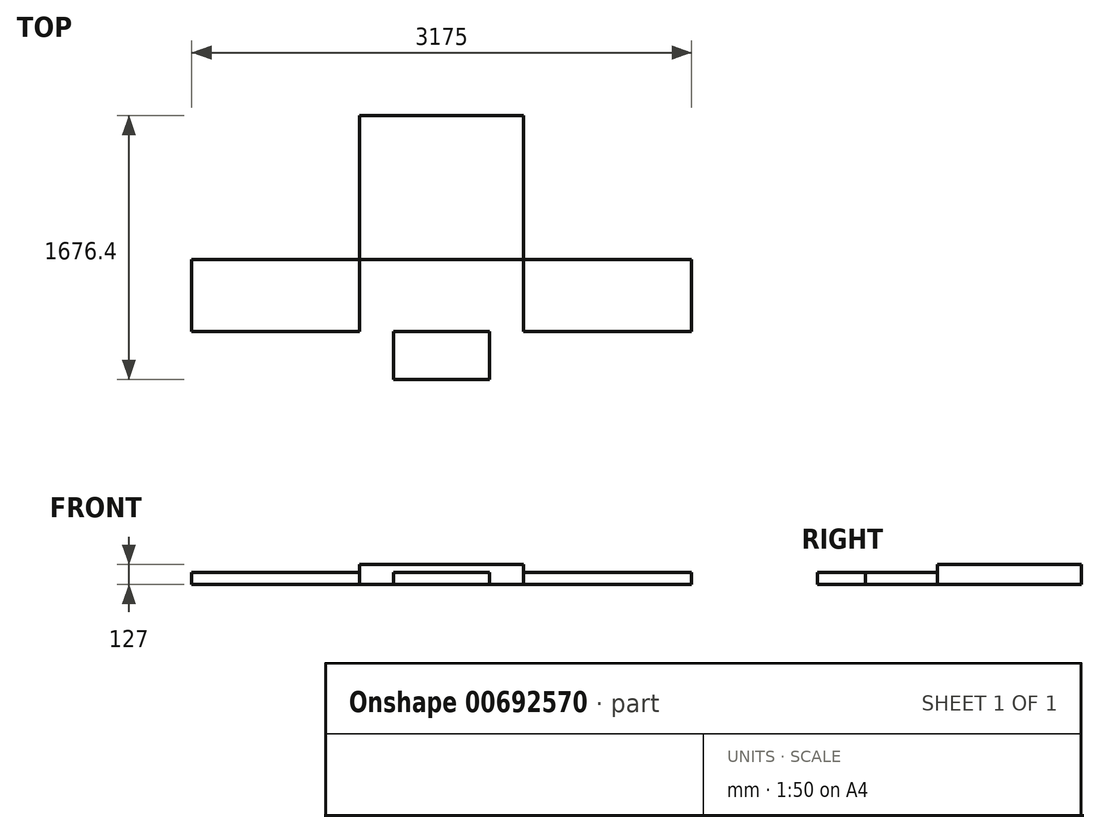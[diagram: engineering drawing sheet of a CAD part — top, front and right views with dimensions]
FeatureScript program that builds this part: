
annotation { "Feature Type Name" : "Feature", "Feature Type Description" : "" }
export const myFeature = defineFeature(function(context is Context, id is Id, definition is map)
    precondition{}
    {
        {
            var Q0;
            Q0=qCreatedBy(makeId("Top.planeOp"),FACE);
            var sketch = newSketch(context, id + "F0", { "sketchPlane" : qUnion([Q0])});
            skLineSegment(sketch, "E0.bottom", {"start": v(0, 0) * mm, "end": v(1041.4, 0) * mm});
            skLineSegment(sketch, "E0.top", {"start": v(0, 914.4) * mm, "end": v(1041.4, 914.4) * mm});
            skLineSegment(sketch, "E0.left", {"start": v(0, 0) * mm, "end": v(0, 914.4) * mm});
            skLineSegment(sketch, "E0.right", {"start": v(1041.4, 0) * mm, "end": v(1041.4, 914.4) * mm});
            skSolve(sketch);
        }
        {
            var Q0;
            Q0 = qSketchRegion(id + "F0", true);
            extrude(context, id + "F1", {"entities" : qUnion([Q0]), "depth" : 127 * mm, "offsetDistance" : 25.4 * mm});
        }
        {
            var Q0;
            Q0=makeQuery(id+"F1.opExtrude","CAP_FACE",FACE,{"disambiguationData":[OSD([sQuery(id+"F0.wireOp",EDGE,"E0.bottom"),sQuery(id+"F0.wireOp",EDGE,"E0.top"),sQuery(id+"F0.wireOp",EDGE,"E0.left"),sQuery(id+"F0.wireOp",EDGE,"E0.right")])],"isStart":false});
            var sketch = newSketch(context, id + "F2", { "sketchPlane" : qUnion([Q0])});
            skLineSegment(sketch, "E1.bottom", {"start": v(0, 0) * mm, "end": v(-1066.8, 0) * mm});
            skLineSegment(sketch, "E1.top", {"start": v(0, -457.2) * mm, "end": v(-1066.8, -457.2) * mm});
            skLineSegment(sketch, "E1.left", {"start": v(0, 0) * mm, "end": v(0, -457.2) * mm});
            skLineSegment(sketch, "E1.right", {"start": v(-1066.8, 0) * mm, "end": v(-1066.8, -457.2) * mm});
            skLineSegment(sketch, "E2.bottom", {"start": v(1041.4, 0) * mm, "end": v(2108.2, 0) * mm});
            skLineSegment(sketch, "E2.top", {"start": v(1041.4, -457.2) * mm, "end": v(2108.2, -457.2) * mm});
            skLineSegment(sketch, "E2.left", {"start": v(1041.4, 0) * mm, "end": v(1041.4, -457.2) * mm});
            skLineSegment(sketch, "E2.right", {"start": v(2108.2, 0) * mm, "end": v(2108.2, -457.2) * mm});
            skSolve(sketch);
        }
        {
            var Q0;
            Q0 = qSketchRegion(id + "F2", true);
            extrude(context, id + "F3", {"entities" : qUnion([Q0]), "oppositeDirection" : true, "depth" : 127 * mm, "offsetDistance" : 25.4 * mm, "hasSecondDirection" : true, "secondDirectionOppositeDirection" : true, "secondDirectionDepth" : 50.8 * mm});
        }
        {
            var Q0;
            Q0=makeQuery(id+"F1.opExtrude","CAP_FACE",FACE,{"disambiguationData":[OSD([sQuery(id+"F0.wireOp",EDGE,"E0.bottom"),sQuery(id+"F0.wireOp",EDGE,"E0.top"),sQuery(id+"F0.wireOp",EDGE,"E0.left"),sQuery(id+"F0.wireOp",EDGE,"E0.right")])],"isStart":false});
            var sketch = newSketch(context, id + "F4", { "sketchPlane" : qUnion([Q0])});
            skPoint(sketch, "E3", {"position": v(520.7, -609.6) * mm});
            skPoint(sketch, "E3.positionSnap0", {"position": v(520.7, 0) * mm});
            skLineSegment(sketch, "E4.bottom", {"start": v(825.5, -457.2) * mm, "end": v(215.9, -457.2) * mm});
            skLineSegment(sketch, "E4.top", {"start": v(825.5, -762) * mm, "end": v(215.9, -762) * mm});
            skLineSegment(sketch, "E4.left", {"start": v(825.5, -457.2) * mm, "end": v(825.5, -762) * mm});
            skLineSegment(sketch, "E4.right", {"start": v(215.9, -457.2) * mm, "end": v(215.9, -762) * mm});
            skSolve(sketch);
        }
        {
            var Q0;
            Q0 = qSketchRegion(id + "F4", true);
            extrude(context, id + "F5", {"entities" : qUnion([Q0]), "oppositeDirection" : true, "depth" : 127 * mm, "offsetDistance" : 25.4 * mm, "hasSecondDirection" : true, "secondDirectionOppositeDirection" : true, "secondDirectionDepth" : 50.8 * mm});
        }
    });
